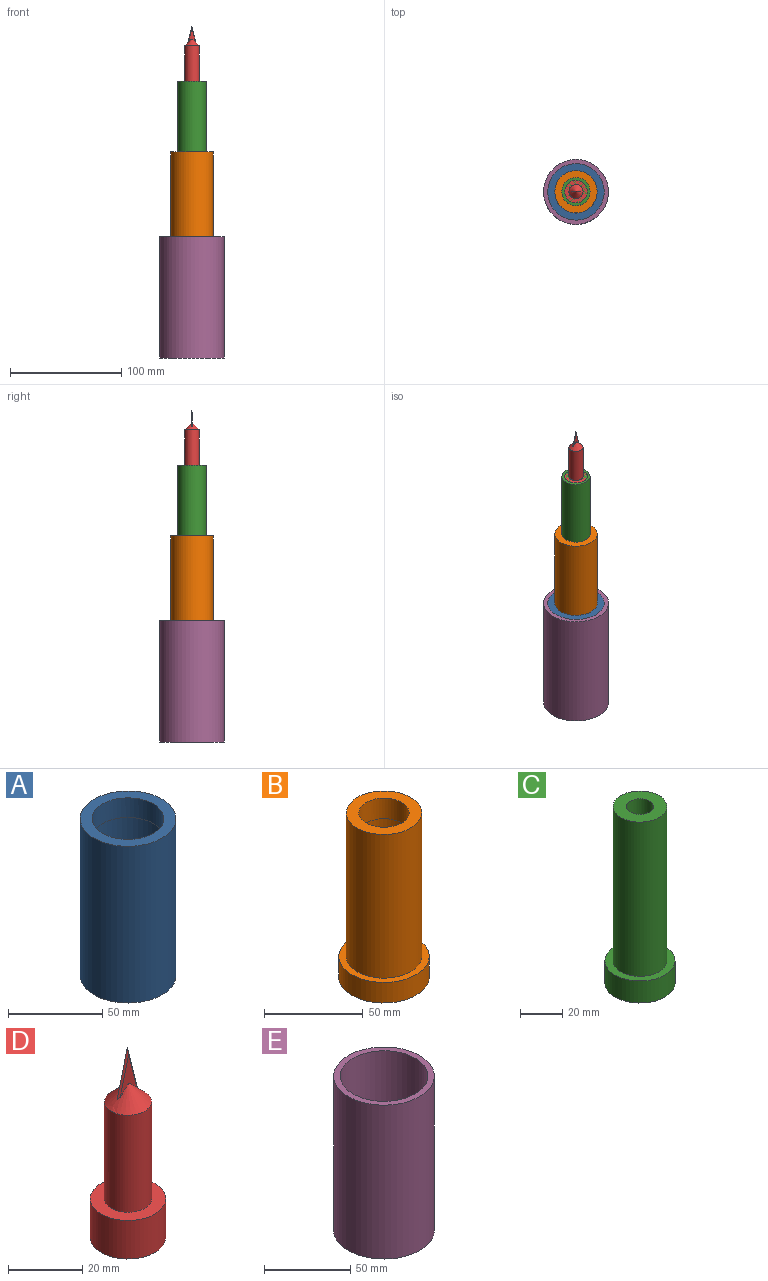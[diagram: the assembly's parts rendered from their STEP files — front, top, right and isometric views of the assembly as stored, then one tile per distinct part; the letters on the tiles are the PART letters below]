
ASSEMBLY  parts=5 mates=6
PART A: 6 faces, bbox 50.8x50.8x101.6 mm
  f0: cylinder r=19.05mm len=38.1mm, axis (0,0,1), area 1520.1mm2, adj f2,f4
  f1: cylinder r=25.4mm len=101.6mm, axis (0,0,-1), area 16214.6mm2, adj f2,f3
  f2: plane 50.8x50.8mm, normal (0,0,1), area 886.7mm2, adj f0,f1
  f3: plane 50.8x50.8mm, normal (0,0,-1), area 385.1mm2, adj f1,f5
  f4: plane 45.72x45.72mm, normal (0,0,-1), area 501.6mm2, adj f0,f5
  f5: cylinder r=22.86mm len=88.9mm, axis (0,0,-1), area 12769mm2, adj f3,f4
PART B: 8 faces, bbox 45.7x45.7x101.6 mm
  f0: cylinder r=12.7mm len=25.4mm, axis (0,0,1), area 1013.4mm2, adj f2,f7
  f1: cylinder r=19.05mm len=88.9mm, axis (0,0,-1), area 10640.9mm2, adj f2,f5
  f2: plane 38.1x38.1mm, normal (0,0,1), area 633.4mm2, adj f0,f1
  f3: cylinder r=22.86mm len=45.72mm, axis (0,0,1), area 1824.1mm2, adj f4,f5
  f4: plane 45.72x45.72mm, normal (0,0,-1), area 785.4mm2, adj f3,f6
  f5: plane 45.72x45.72mm, normal (0,0,1), area 501.6mm2, adj f1,f3
  f6: cylinder r=16.51mm len=88.9mm, axis (0,0,-1), area 9222.1mm2, adj f4,f7
  f7: plane 33.02x33.02mm, normal (0,0,-1), area 349.6mm2, adj f0,f6
PART C: 8 faces, bbox 33x33x101.6 mm
  f0: cylinder r=6.35mm len=12.7mm, axis (0,0,-1), area 506.7mm2, adj f2,f4
  f1: cylinder r=12.7mm len=88.9mm, axis (0,0,-1), area 7093.9mm2, adj f2,f5
  f2: plane 25.4x25.4mm, normal (0,0,1), area 380mm2, adj f0,f1
  f3: cylinder r=10.16mm len=88.9mm, axis (0,0,-1), area 5675.1mm2, adj f4,f6
  f4: plane 20.32x20.32mm, normal (0,0,-1), area 197.6mm2, adj f0,f3
  f5: plane 33.02x33.02mm, normal (0,0,1), area 349.6mm2, adj f1,f7
  f6: plane 33.02x33.02mm, normal (0,0,-1), area 532mm2, adj f3,f7
  f7: cylinder r=16.51mm len=33.02mm, axis (0,0,1), area 1317.4mm2, adj f5,f6
PART D: 10 faces, bbox 20.3x20.3x62.6 mm
  f0: plane 15.39x3.85mm, normal (0.69,-0.71,0.17), area 10.4mm2, adj f1,f2,f3,f5
  f1: plane 12.6x6.3mm, normal (0,-1,0), area 29.9mm2, adj f0,f2,f5
  f2: plane 15.39x3.85mm, normal (-0.69,-0.71,0.17), area 10.4mm2, adj f0,f1,f3,f5
  f3: plane 15.39x7.69mm, normal (0,1,0), area 44.6mm2, adj f0,f2,f4,f5
  f4: cone r=0.25mm half-angle=45deg, axis (0,0,-1), area 0mm2, adj f3,f5
  f5: cone r=0.25mm half-angle=45deg, axis (0,0,-1), area 174.1mm2, adj f0,f1,f2,f3,f4,f6
  f6: cylinder r=6.35mm len=32mm, axis (0,0,-1), area 1276.9mm2, adj f5,f7
  f7: plane 20.32x20.32mm, normal (0,0,1), area 197.6mm2, adj f6,f8
  f8: cylinder r=10.16mm len=20.32mm, axis (0,0,1), area 810.7mm2, adj f7,f9
  f9: plane 20.32x20.32mm, normal (0,0,-1), area 324.3mm2, adj f8
PART E: 5 faces, bbox 58.4x58.4x109.2 mm
  f0: cylinder r=25.4mm len=101.6mm, axis (0,0,1), area 16214.6mm2, adj f1,f2
  f1: plane 50.8x50.8mm, normal (0,0,1), area 2026.8mm2, adj f0
  f2: plane 58.42x58.42mm, normal (0,0,1), area 653.7mm2, adj f0,f4
  f3: plane 58.42x58.42mm, normal (0,0,-1), area 2680.5mm2, adj f4
  f4: cylinder r=29.21mm len=109.22mm, axis (0,0,-1), area 20045.3mm2, adj f2,f3
PLACE A rot(axis=(0,0,1),0deg) t=(426.63,-460.99,-1482.45)mm
PLACE B rot(axis=(0,0,1),0deg) t=(426.63,-460.99,-1406.25)mm
PLACE C rot(axis=(0,0,1),0deg) t=(426.63,-460.99,-1342.75)mm
PLACE D rot(axis=(0,0,1),0deg) t=(426.63,-460.99,-1241.15)mm
PLACE E rot(axis=(0,0,1),0deg) t=(426.63,-460.99,-1490.07)mm
MATE slider C.f7 <-> B.f6  axis (0,0,-1) through (426.63,-460.99,-1342.75)mm
MATE fastened A.f1 <-> E.f0  axis (0,0,-1) through (426.63,-460.99,-1482.45)mm
MATE slider D.f8 <-> C.f3  axis (0,0,-1) through (426.63,-460.99,-1253.85)mm
MATE slider D.f8 <-> C.f0  axis (0,0,-1) through (426.63,-460.99,-1253.85)mm
MATE slider B.f3 <-> A.f5  axis (0,0,-1) through (426.63,-460.99,-1406.25)mm
MATE slider D.f8 <-> C.f0  axis (0,0,-1) through (426.63,-460.99,-1253.85)mm
